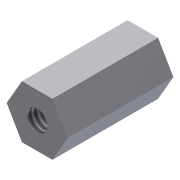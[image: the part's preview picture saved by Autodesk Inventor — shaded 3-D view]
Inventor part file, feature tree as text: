
AUTODESK INVENTOR PART (.ipt)
format: ipt  version: 2013 (Build 170138000, 138)  size: 77,312 bytes
history: native  units: in
note: dims shown in document units (in); Inventor stores cm internally (conversion verified against a paired STEP export)
features: sketch x2, extrude x1, hole x1
ambient origin geometry x8: Origin, YZ Plane, XZ Plane, XY Plane, X Axis, Y Axis, Z Axis, Center Point
bodies: Solid1 (feature_tree)
feature tree (4):
  extrude  "Extrusion1"  Depth=1.0in TaperAngle=0.0deg
  hole  "Hole1"  [1 undecoded]
  sketch  "Sketch1"  dims[d0=0.5in d1=1.0in d2=0.0in]
  sketch  "Sketch2"  dims[d3=0.196in d4=0.75in d5=0.375in d6=0.25in d7=0.5635in d8=1.0in d9=0.8108in]
note: 1 required parameter value undecoded (feature->parameter linkage not recoverable at this tier; creation-order binding heuristic only, values carry confidence <= 0.55)
